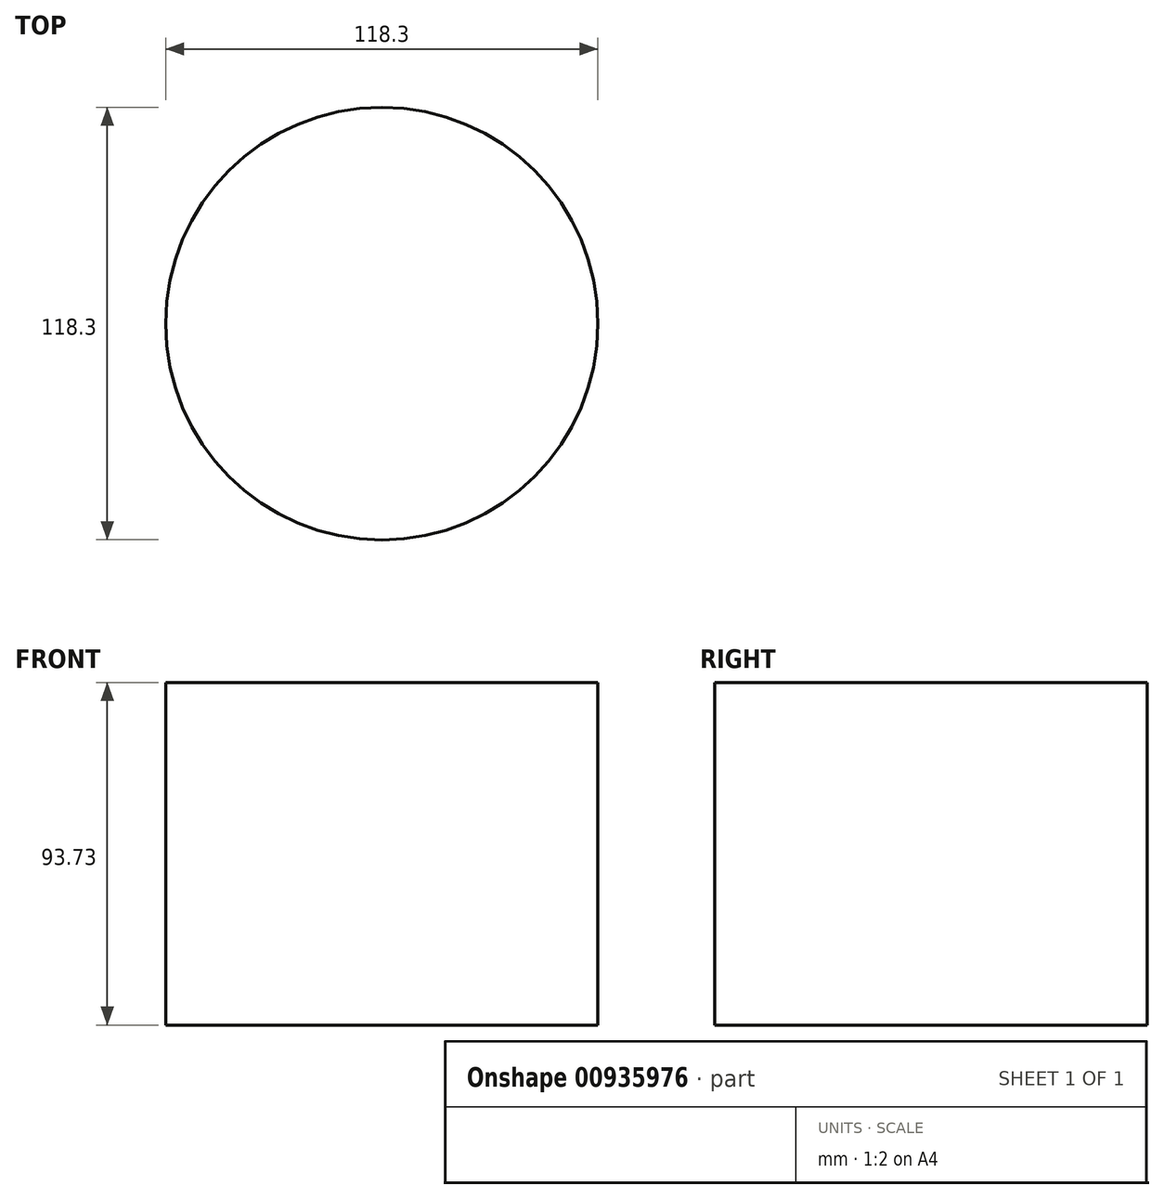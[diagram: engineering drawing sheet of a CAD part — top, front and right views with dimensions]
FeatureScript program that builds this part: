
annotation { "Feature Type Name" : "Feature", "Feature Type Description" : "" }
export const myFeature = defineFeature(function(context is Context, id is Id, definition is map)
    precondition{}
    {
        {
            var Q0;
            Q0=qCreatedBy(makeId("Top.planeOp"),FACE);
            var sketch = newSketch(context, id + "F0", { "sketchPlane" : qUnion([Q0])});
            skCircle(sketch, "E0", {"center": v(0, 0) * mm, "radius": 59.15 * mm});
            skSolve(sketch);
        }
        {
            var Q0;
            Q0=makeQuery(id+"F0.imprint","IMPRINT",FACE,{"disambiguationData":[TD([[makeQuery(id+"F0.imprint","IMPRINT",EDGE,{"derivedFrom":sQuery(id+"F0.wireOp",EDGE,"E0")}),1.0]])]});
            extrude(context, id + "F1", {"entities" : qUnion([Q0]), "depth" : 93.73 * mm, "offsetDistance" : 25.4 * mm});
        }
    });
